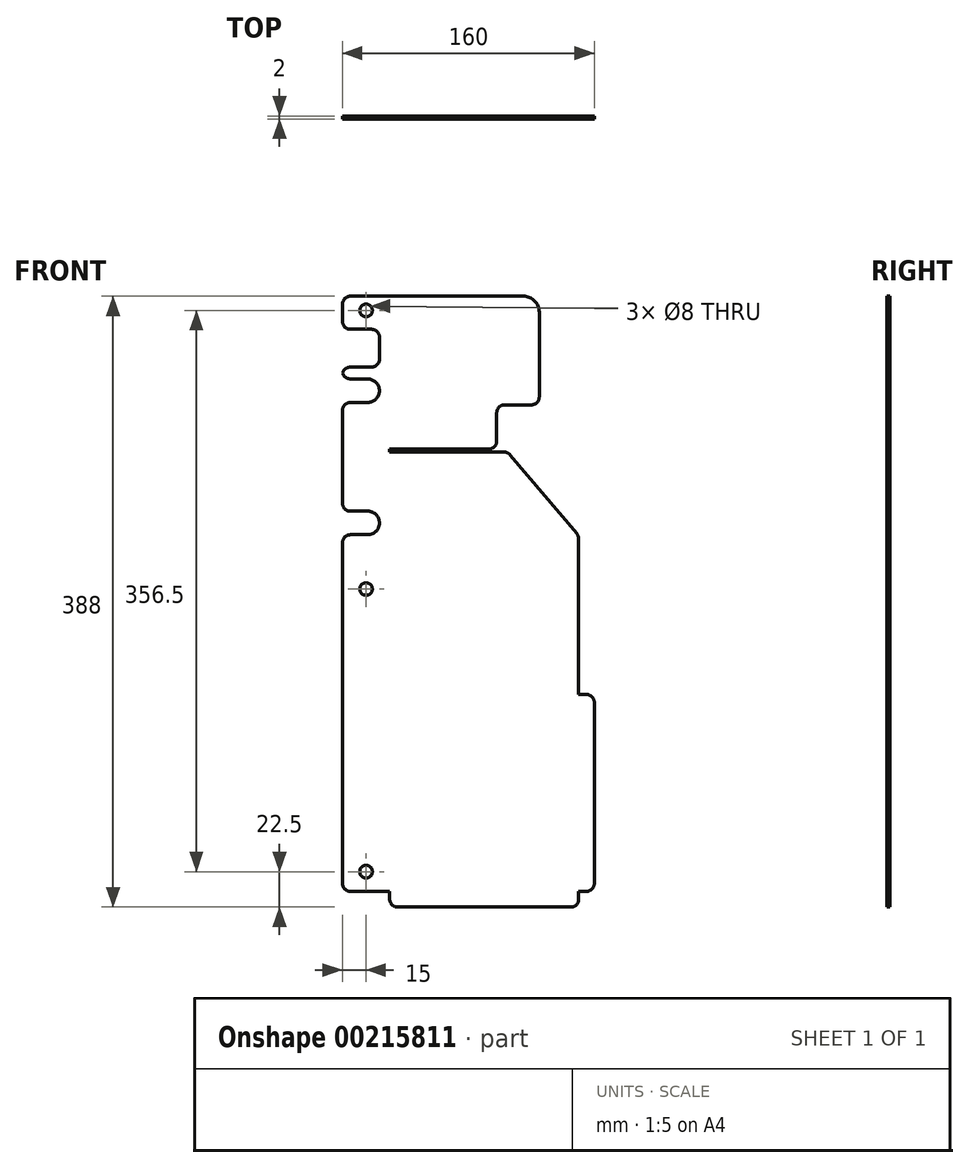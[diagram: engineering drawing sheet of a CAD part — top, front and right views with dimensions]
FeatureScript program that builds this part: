
annotation { "Feature Type Name" : "Feature", "Feature Type Description" : "" }
export const myFeature = defineFeature(function(context is Context, id is Id, definition is map)
    precondition{}
    {
        {
            var Q0;
            Q0=qCreatedBy(makeId("Front.planeOp"),FACE);
            var sketch = newSketch(context, id + "F0", { "sketchPlane" : qUnion([Q0])});
            skLineSegment(sketch, "E0", {"start": v(5, 378) * mm, "end": v(85, 378) * mm});
            skLineSegment(sketch, "E1", {"start": v(95, 368) * mm, "end": v(95, 314.01) * mm});
            skLineSegment(sketch, "E2", {"start": v(90, 309.01) * mm, "end": v(73, 309.01) * mm});
            skLineSegment(sketch, "E3", {"start": v(68, 304.01) * mm, "end": v(68, 286) * mm});
            skLineSegment(sketch, "E4", {"start": v(63, 281) * mm, "end": v(0, 281) * mm});
            skLineSegment(sketch, "E5", {"start": v(0, 279) * mm, "end": v(72.68, 279) * mm});
            skLineSegment(sketch, "E6", {"start": v(76.5, 277.23) * mm, "end": v(118.82, 227.22) * mm});
            skLineSegment(sketch, "E7", {"start": v(120, 223.99) * mm, "end": v(120, 0) * mm});
            skLineSegment(sketch, "E8", {"start": v(120, 0) * mm, "end": v(0, 0) * mm});
            skLineSegment(sketch, "E9", {"start": v(0, 0) * mm, "end": v(-25, 0) * mm});
            skLineSegment(sketch, "E10", {"start": v(-30, 5) * mm, "end": v(-30, 221.5) * mm});
            skLineSegment(sketch, "E11", {"start": v(-25, 378) * mm, "end": v(5, 378) * mm});
            skLineSegment(sketch, "E12", {"start": v(120, 125) * mm, "end": v(125, 125) * mm});
            skLineSegment(sketch, "E13", {"start": v(130, 120) * mm, "end": v(130, 5) * mm});
            skLineSegment(sketch, "E14", {"start": v(125, 0) * mm, "end": v(120, 0) * mm});
            skLineSegment(sketch, "E15", {"start": v(120, 0) * mm, "end": v(120, -5) * mm});
            skLineSegment(sketch, "E16", {"start": v(115, -10) * mm, "end": v(5, -10) * mm});
            skLineSegment(sketch, "E17", {"start": v(0, -5) * mm, "end": v(0, 0) * mm});
            skLineSegment(sketch, "E18", {"start": v(-25, 357) * mm, "end": v(-11.5, 357) * mm});
            skLineSegment(sketch, "E19", {"start": v(-25, 333) * mm, "end": v(-11.5, 333) * mm});
            skLineSegment(sketch, "E20.trimOffspring", {"start": v(-30, 362) * mm, "end": v(-30, 373) * mm});
            skPoint(sketch, "E21.newPointA", {"position": v(0, 357) * mm});
            skPoint(sketch, "E21.newPointB", {"position": v(0, 378) * mm});
            skPoint(sketch, "E22.newPointA", {"position": v(0, 0) * mm});
            skPoint(sketch, "E23.visualSharp", {"position": v(-30, 333) * mm});
            skArc(sketch, "E23.filletArc", {"start": v(-25, 333) * mm, "mid": v(-28.54, 331.54) * mm, "end": v(-30, 328) * mm});
            skPoint(sketch, "E24.visualSharp", {"position": v(-30, 357) * mm});
            skArc(sketch, "E24.filletArc", {"start": v(-30, 362) * mm, "mid": v(-28.54, 358.46) * mm, "end": v(-25, 357) * mm});
            skPoint(sketch, "E25.visualSharp", {"position": v(-30, 378) * mm});
            skArc(sketch, "E25.filletArc", {"start": v(-25, 378) * mm, "mid": v(-28.54, 376.54) * mm, "end": v(-30, 373) * mm});
            skPoint(sketch, "E26.visualSharp", {"position": v(95, 378) * mm});
            skArc(sketch, "E26.filletArc", {"start": v(95, 368) * mm, "mid": v(92.07, 375.07) * mm, "end": v(85, 378) * mm});
            skPoint(sketch, "E27.visualSharp", {"position": v(95, 309.01) * mm});
            skArc(sketch, "E27.filletArc", {"start": v(90, 309.01) * mm, "mid": v(93.54, 310.48) * mm, "end": v(95, 314.01) * mm});
            skPoint(sketch, "E28.visualSharp", {"position": v(68, 309.01) * mm});
            skArc(sketch, "E28.filletArc", {"start": v(73, 309.01) * mm, "mid": v(69.46, 307.55) * mm, "end": v(68, 304.01) * mm});
            skPoint(sketch, "E29.visualSharp", {"position": v(68, 281) * mm});
            skArc(sketch, "E29.filletArc", {"start": v(63, 281) * mm, "mid": v(66.54, 282.46) * mm, "end": v(68, 286) * mm});
            skPoint(sketch, "E30.visualSharp", {"position": v(75, 279) * mm});
            skArc(sketch, "E30.filletArc", {"start": v(76.5, 277.23) * mm, "mid": v(74.78, 278.54) * mm, "end": v(72.68, 279) * mm});
            skPoint(sketch, "E31.visualSharp", {"position": v(120, 225.82) * mm});
            skArc(sketch, "E31.filletArc", {"start": v(120, 223.99) * mm, "mid": v(119.7, 225.7) * mm, "end": v(118.82, 227.22) * mm});
            skPoint(sketch, "E32.visualSharp", {"position": v(130, 125) * mm});
            skArc(sketch, "E32.filletArc", {"start": v(130, 120) * mm, "mid": v(128.54, 123.54) * mm, "end": v(125, 125) * mm});
            skPoint(sketch, "E33.visualSharp", {"position": v(130, 0) * mm});
            skArc(sketch, "E33.filletArc", {"start": v(125, 0) * mm, "mid": v(128.54, 1.46) * mm, "end": v(130, 5) * mm});
            skPoint(sketch, "E34.visualSharp", {"position": v(120, -10) * mm});
            skArc(sketch, "E34.filletArc", {"start": v(115, -10) * mm, "mid": v(118.54, -8.54) * mm, "end": v(120, -5) * mm});
            skPoint(sketch, "E35.visualSharp", {"position": v(0, -10) * mm});
            skArc(sketch, "E35.filletArc", {"start": v(0, -5) * mm, "mid": v(1.46, -8.54) * mm, "end": v(5, -10) * mm});
            skPoint(sketch, "E36.visualSharp", {"position": v(-30, 0) * mm});
            skArc(sketch, "E36.filletArc", {"start": v(-30, 5) * mm, "mid": v(-28.54, 1.46) * mm, "end": v(-25, 0) * mm});
            skCircle(sketch, "E37", {"center": v(-15, 369) * mm, "radius": 4 * mm});
            skArc(sketch, "E38", {"start": v(-14, 310.5) * mm, "mid": v(-6.5, 318) * mm, "end": v(-14, 325.5) * mm});
            skLineSegment(sketch, "E39", {"start": v(-14, 310.5) * mm, "end": v(-25, 310.5) * mm});
            skLineSegment(sketch, "E40", {"start": v(-14, 325.5) * mm, "end": v(-25, 325.5) * mm});
            skLineSegment(sketch, "E41.trimOffspring", {"start": v(-30, 328) * mm, "end": v(-30, 330.5) * mm});
            skPoint(sketch, "E42.visualSharp", {"position": v(-30, 325.5) * mm});
            skArc(sketch, "E42.filletArc", {"start": v(-30, 330.5) * mm, "mid": v(-28.54, 326.96) * mm, "end": v(-25, 325.5) * mm});
            skPoint(sketch, "E43.visualSharp", {"position": v(-30, 310.5) * mm});
            skArc(sketch, "E43.filletArc", {"start": v(-25, 310.5) * mm, "mid": v(-28.54, 309.04) * mm, "end": v(-30, 305.5) * mm});
            skArc(sketch, "E44", {"start": v(-14.27, 226.5) * mm, "mid": v(-6.5, 233.88) * mm, "end": v(-14.03, 241.5) * mm});
            skLineSegment(sketch, "E45", {"start": v(-14.27, 226.5) * mm, "end": v(-25, 226.5) * mm});
            skLineSegment(sketch, "E46", {"start": v(-13.97, 241.5) * mm, "end": v(-25, 241.5) * mm});
            skLineSegment(sketch, "E47.trimOffspring", {"start": v(-30, 246.5) * mm, "end": v(-30, 305.5) * mm});
            skPoint(sketch, "E48.visualSharp", {"position": v(-30, 241.5) * mm});
            skArc(sketch, "E48.filletArc", {"start": v(-30, 246.5) * mm, "mid": v(-28.54, 242.96) * mm, "end": v(-25, 241.5) * mm});
            skPoint(sketch, "E49.visualSharp", {"position": v(-30, 226.5) * mm});
            skArc(sketch, "E49.filletArc", {"start": v(-25, 226.5) * mm, "mid": v(-28.54, 225.04) * mm, "end": v(-30, 221.5) * mm});
            skCircle(sketch, "E50", {"center": v(-15, 192) * mm, "radius": 4 * mm});
            skCircle(sketch, "E51", {"center": v(-15, 12.5) * mm, "radius": 4 * mm});
            skLineSegment(sketch, "E52", {"start": v(-6.5, 352) * mm, "end": v(-6.5, 338) * mm});
            skPoint(sketch, "E53.visualSharp", {"position": v(-6.5, 357) * mm});
            skArc(sketch, "E53.filletArc", {"start": v(-6.5, 352) * mm, "mid": v(-7.96, 355.54) * mm, "end": v(-11.5, 357) * mm});
            skPoint(sketch, "E54.visualSharp", {"position": v(-6.5, 333) * mm});
            skArc(sketch, "E54.filletArc", {"start": v(-11.5, 333) * mm, "mid": v(-7.96, 334.46) * mm, "end": v(-6.5, 338) * mm});
            skLineSegment(sketch, "E55", {"start": v(0, 279) * mm, "end": v(0, 281) * mm});
            skSolve(sketch);
        }
        {
            var Q0;
            {var subQ1=sQuery(id+"F0.wireOp",EDGE,"E12");Q0=makeQuery(id+"F0.imprint","IMPRINT",FACE,{"disambiguationData":[TD([[makeQuery(id+"F0.imprint","IMPRINT",EDGE,{"derivedFrom":subQ1}),-1.0]])]});}
            var Q1;
            Q1=makeQuery(id+"F0.imprint","IMPRINT",FACE,{"disambiguationData":[TD([[makeQuery(id+"F0.imprint","IMPRINT",EDGE,{"derivedFrom":sQuery(id+"F0.wireOp",EDGE,"E8")}),1.0]])]});
            var Q2;
            Q2=makeQuery(id+"F0.imprint","IMPRINT",FACE,{"disambiguationData":[TD([[makeQuery(id+"F0.imprint","IMPRINT",EDGE,{"derivedFrom":sQuery(id+"F0.wireOp",EDGE,"E0")}),-1.0]])]});
            extrude(context, id + "F1", {"entities" : qUnion([Q0, Q1, Q2]), "depth" : 2 * mm});
        }
    });
